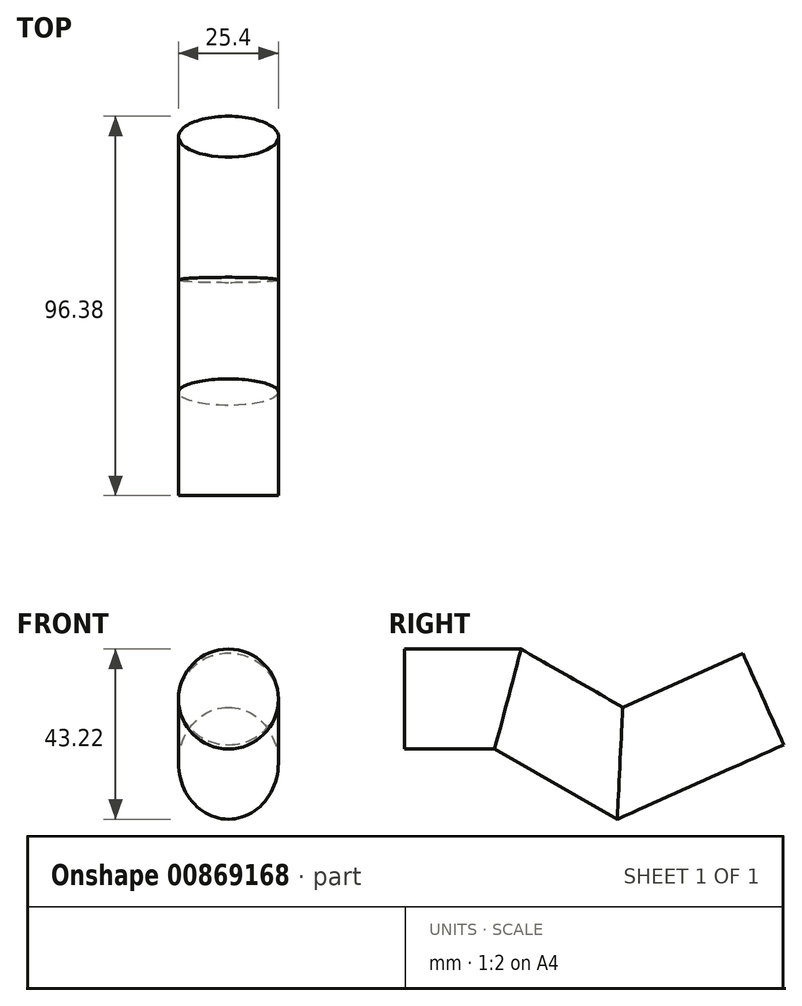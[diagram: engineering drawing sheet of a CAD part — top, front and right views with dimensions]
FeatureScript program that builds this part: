
annotation { "Feature Type Name" : "Feature", "Feature Type Description" : "" }
export const myFeature = defineFeature(function(context is Context, id is Id, definition is map)
    precondition{}
    {
        {
            var Q0;
            Q0=qCreatedBy(makeId("Front.planeOp"),FACE);
            var sketch = newSketch(context, id + "F0", { "sketchPlane" : qUnion([Q0])});
            skCircle(sketch, "E0", {"center": v(0, 0) * mm, "radius": 12.7 * mm});
            skSolve(sketch);
        }
        {
            var Q0;
            Q0=qCreatedBy(makeId("Right.planeOp"),FACE);
            var sketch = newSketch(context, id + "F1", { "sketchPlane" : qUnion([Q0])});
            skLineSegment(sketch, "E1", {"start": v(0, 0) * mm, "end": v(26.29, 0) * mm});
            skLineSegment(sketch, "E2", {"start": v(26.29, 0) * mm, "end": v(54.77, -16.3) * mm});
            skLineSegment(sketch, "E3", {"start": v(54.77, -16.3) * mm, "end": v(91.2, 0) * mm});
            skSolve(sketch);
        }
        {
            var Q0;
            Q0 = qSketchRegion(id + "F0", true);
            var Q1;
            Q1=sQuery(id+"F1.wireOp",EDGE,"E1");
            var Q2;
            Q2=sQuery(id+"F1.wireOp",EDGE,"E2");
            var Q3;
            Q3=sQuery(id+"F1.wireOp",EDGE,"E3");
            sweep(context, id + "F2", {"profiles" : qUnion([Q0]), "path" : qUnion([Q1, Q2, Q3])});
        }
    });
